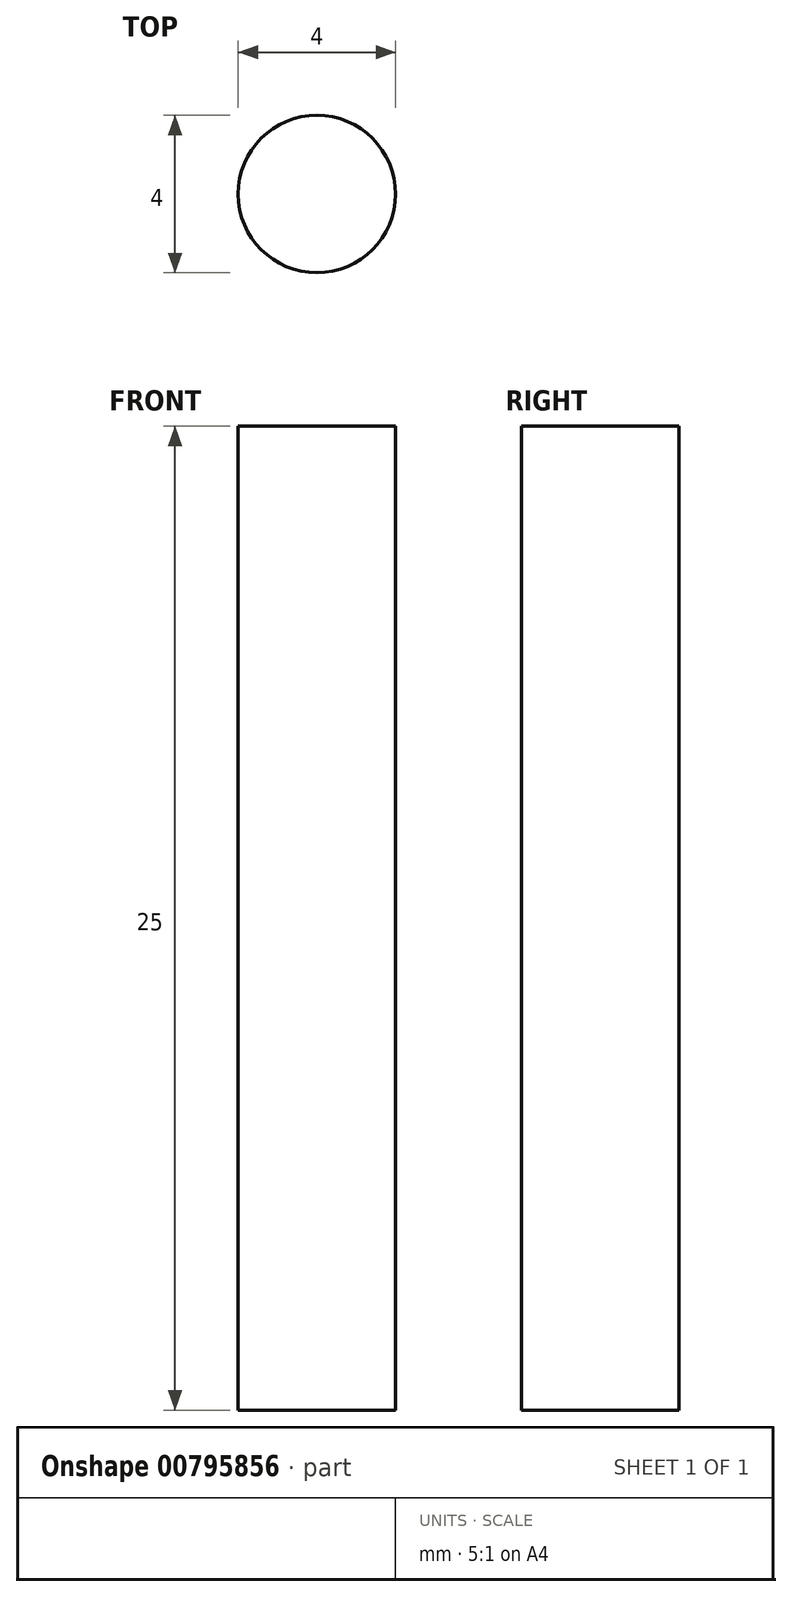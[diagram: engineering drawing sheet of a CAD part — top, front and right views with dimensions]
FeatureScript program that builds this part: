
annotation { "Feature Type Name" : "Feature", "Feature Type Description" : "" }
export const myFeature = defineFeature(function(context is Context, id is Id, definition is map)
    precondition{}
    {
        {
            var Q0;
            Q0=qCreatedBy(makeId("Front.planeOp"),FACE);
            var sketch = newSketch(context, id + "F0", { "sketchPlane" : qUnion([Q0])});
            skLineSegment(sketch, "E0.bottom", {"start": v(0, 12.5) * mm, "end": v(2, 12.5) * mm});
            skLineSegment(sketch, "E0.top", {"start": v(0, -12.5) * mm, "end": v(2, -12.5) * mm});
            skLineSegment(sketch, "E0.left", {"start": v(0, 12.5) * mm, "end": v(0, -12.5) * mm});
            skLineSegment(sketch, "E0.right", {"start": v(2, 12.5) * mm, "end": v(2, -12.5) * mm});
            skSolve(sketch);
        }
        {
            var Q0;
            Q0 = qSketchRegion(id + "F0", true);
            var Q1;
            Q1=sQuery(id+"F0.wireOp",EDGE,"E0.left");
            revolve(context, id + "F1", {"surfaceOperationType" : NewSurfaceOperationType.NEW, "entities" : qUnion([Q0]), "axis" : qUnion([Q1]), "revolveType" : RevolveType.FULL});
        }
    });
